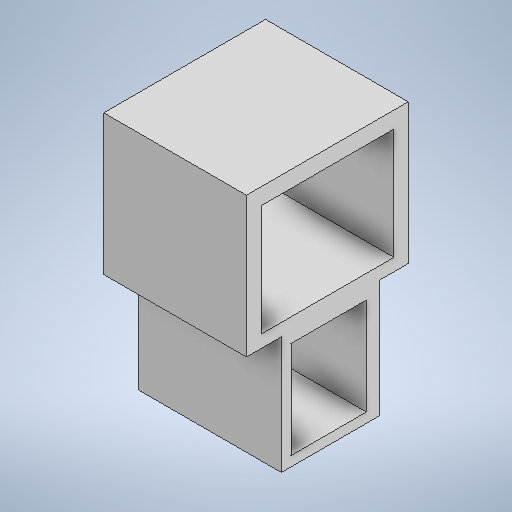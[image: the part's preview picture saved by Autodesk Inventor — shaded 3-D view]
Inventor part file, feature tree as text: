
AUTODESK INVENTOR PART (.ipt)
format: ipt  version: 2025.1 (Build 291241000, 241)  size: 220,672 bytes
history: native  units: in
note: dims shown in document units (in); Inventor stores cm internally (conversion verified against a paired STEP export)
features: sketch x5, extrude x4
ambient origin geometry x8: Origin, YZ Plane, XZ Plane, XY Plane, X Axis, Y Axis, Z Axis, Center Point
bodies: Solid1 (feature_tree)
feature tree (9):
  extrude  "Extrusion1"  Depth=1.0in TaperAngle=0.0deg
  extrude  "Extrusion2"  Depth=1.0in TaperAngle=0.0deg
  extrude  "Extrusion3"  Depth=0.0344in
  extrude  "Extrusion4"  Depth=0.0344in
  sketch  "Sketch6"
  sketch  "Sketch1"  dims[d0=1.0in d1=0.0in d2=1.0in d3=0.0in]
  sketch  "Sketch2"  dims[d4=1.0in d5=0.0in d6=1.0in d7=0.0in]
  sketch  "Sketch3"  dims[d8=0.5in d9=0.0344in]
  sketch  "Sketch4"  dims[d10=0.5in d11=0.0344in]
